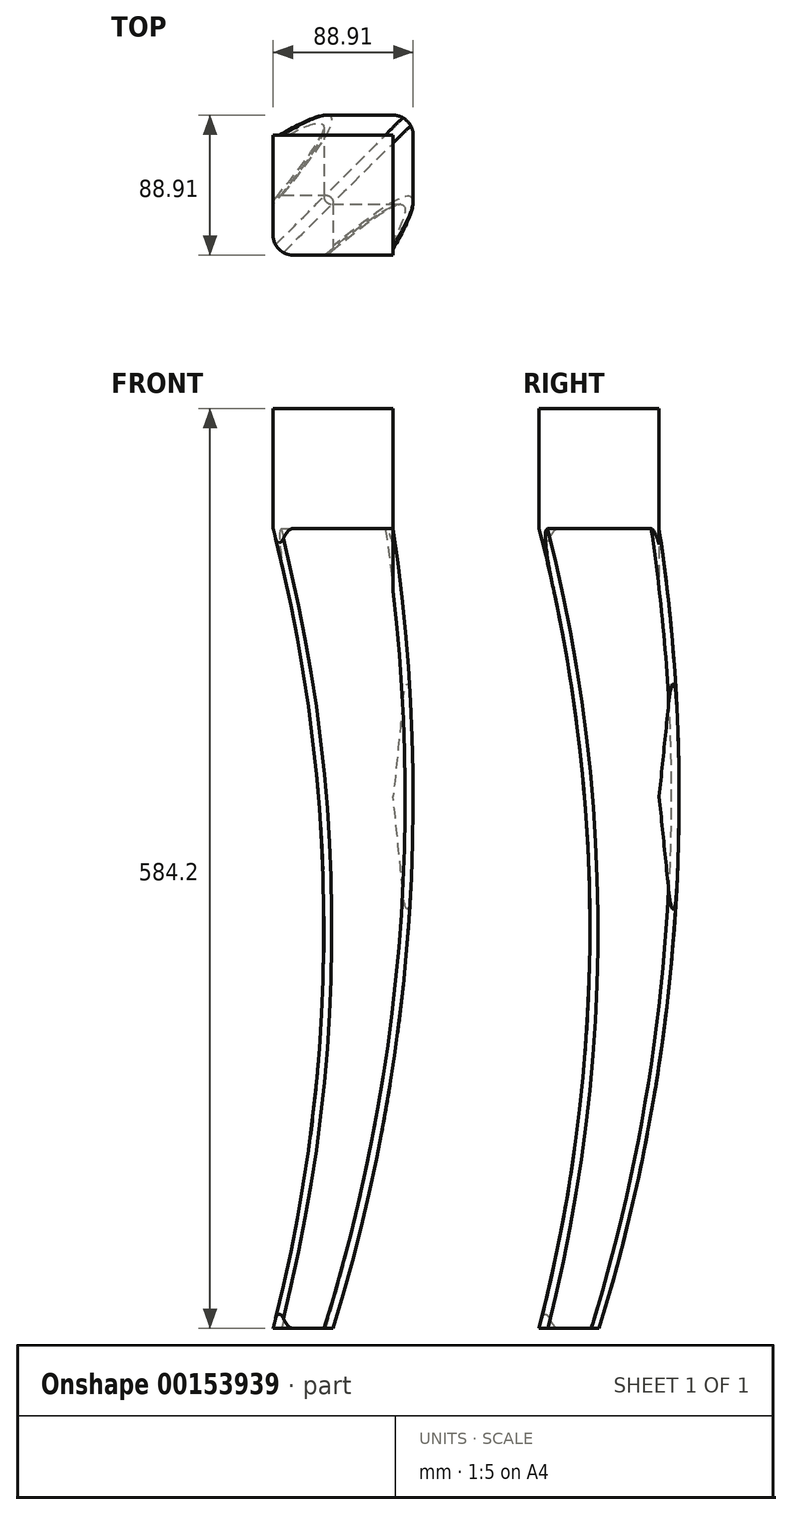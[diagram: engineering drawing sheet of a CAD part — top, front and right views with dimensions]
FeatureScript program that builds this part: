
annotation { "Feature Type Name" : "Feature", "Feature Type Description" : "" }
export const myFeature = defineFeature(function(context is Context, id is Id, definition is map)
    precondition{}
    {
        {
            var Q0;
            Q0=qCreatedBy(makeId("Top.planeOp"),FACE);
            var sketch = newSketch(context, id + "F0", { "sketchPlane" : qUnion([Q0])});
            skLineSegment(sketch, "E0.bottom", {"start": v(31.75, -44.45) * mm, "end": v(-31.75, -44.45) * mm});
            skLineSegment(sketch, "E0.top", {"start": v(31.75, 44.45) * mm, "end": v(-31.75, 44.45) * mm});
            skLineSegment(sketch, "E0.left", {"start": v(44.45, -31.75) * mm, "end": v(44.45, 31.75) * mm});
            skLineSegment(sketch, "E0.right", {"start": v(-44.45, -31.75) * mm, "end": v(-44.45, 31.75) * mm});
            skPoint(sketch, "E0.middle", {"position": v(0, 0) * mm});
            skPoint(sketch, "E1.visualSharp", {"position": v(44.45, -44.45) * mm});
            skArc(sketch, "E1.filletArc", {"start": v(31.75, -44.45) * mm, "mid": v(40.73, -40.73) * mm, "end": v(44.45, -31.75) * mm});
            skPoint(sketch, "E2.visualSharp", {"position": v(44.45, 44.45) * mm});
            skArc(sketch, "E2.filletArc", {"start": v(44.45, 31.75) * mm, "mid": v(40.73, 40.73) * mm, "end": v(31.75, 44.45) * mm});
            skPoint(sketch, "E3.visualSharp", {"position": v(-44.45, 44.45) * mm});
            skArc(sketch, "E3.filletArc", {"start": v(-31.75, 44.45) * mm, "mid": v(-40.73, 40.73) * mm, "end": v(-44.45, 31.75) * mm});
            skPoint(sketch, "E4.visualSharp", {"position": v(-44.45, -44.45) * mm});
            skArc(sketch, "E4.filletArc", {"start": v(-44.45, -31.75) * mm, "mid": v(-40.73, -40.73) * mm, "end": v(-31.75, -44.45) * mm});
            skSolve(sketch);
        }
        {
            var Q0;
            Q0 = qSketchRegion(id + "F0", true);
            extrude(context, id + "F1", {"entities" : qUnion([Q0]), "depth" : 584.2 * mm});
        }
        {
            var Q0;
            Q0=makeQuery(id+"F1.opExtrude","SWEPT_FACE",FACE,{"disambiguationData":[OSD([sQuery(id+"F0.wireOp",EDGE,"E0.left")])]});
            var sketch = newSketch(context, id + "F2", { "sketchPlane" : qUnion([Q0])});
            skArc(sketch, "E5", {"start": v(-44.45, 0) * mm, "mid": v(-12.19, 254) * mm, "end": v(-44.45, 508) * mm});
            skArc(sketch, "E6", {"start": v(-6.35, 0) * mm, "mid": v(41.23, 251.86) * mm, "end": v(31.75, 508) * mm});
            skLineSegment(sketch, "E7", {"start": v(-44.45, 0) * mm, "end": v(-6.35, 0) * mm, "construction": true});
            skLineSegment(sketch, "E8", {"start": v(-44.45, 508) * mm, "end": v(-44.45, 584.2) * mm});
            skLineSegment(sketch, "E9", {"start": v(-44.45, 584.2) * mm, "end": v(31.75, 584.2) * mm, "construction": true});
            skLineSegment(sketch, "E10", {"start": v(31.75, 508) * mm, "end": v(31.75, 584.2) * mm});
            skLineSegment(sketch, "E11", {"start": v(-44.45, 508) * mm, "end": v(31.75, 508) * mm, "construction": true});
            skLineSegment(sketch, "E12", {"start": v(31.75, 584.2) * mm, "end": v(100.82, 584.2) * mm});
            skLineSegment(sketch, "E13", {"start": v(100.82, 584.2) * mm, "end": v(100.82, 0) * mm});
            skLineSegment(sketch, "E14", {"start": v(100.82, 0) * mm, "end": v(-6.35, 0) * mm});
            skLineSegment(sketch, "E15", {"start": v(-44.45, 0) * mm, "end": v(-95.04, 0) * mm});
            skLineSegment(sketch, "E16", {"start": v(-95.04, 0) * mm, "end": v(-95.04, 584.2) * mm});
            skLineSegment(sketch, "E17", {"start": v(-95.04, 584.2) * mm, "end": v(-31.75, 584.2) * mm});
            skSolve(sketch);
        }
        {
            var Q0;
            Q0 = qSketchRegion(id + "F2", true);
            extrude(context, id + "F3", {"entities" : qUnion([Q0]), "operationType" : NewBodyOperationType.REMOVE, "oppositeDirection" : true, "depth" : 101.6 * mm});
        }
        {
            var Q0;
            Q0=makeQuery(id+"F1.opExtrude","SWEPT_FACE",FACE,{"disambiguationData":[OSD([sQuery(id+"F0.wireOp",EDGE,"E0.bottom")])]});
            var sketch = newSketch(context, id + "F4", { "sketchPlane" : qUnion([Q0])});
            skArc(sketch, "E18", {"start": v(-44.45, 0) * mm, "mid": v(-12.19, 254) * mm, "end": v(-44.45, 508) * mm});
            skArc(sketch, "E19", {"start": v(-6.35, 0) * mm, "mid": v(41.23, 251.86) * mm, "end": v(31.75, 508) * mm});
            skLineSegment(sketch, "E20", {"start": v(-44.45, 0) * mm, "end": v(-6.35, 0) * mm, "construction": true});
            skLineSegment(sketch, "E21", {"start": v(-44.45, 508) * mm, "end": v(-44.45, 584.2) * mm});
            skLineSegment(sketch, "E22", {"start": v(-44.45, 584.2) * mm, "end": v(31.75, 584.2) * mm, "construction": true});
            skLineSegment(sketch, "E23", {"start": v(31.75, 508) * mm, "end": v(31.75, 584.2) * mm});
            skLineSegment(sketch, "E24", {"start": v(-44.45, 508) * mm, "end": v(31.75, 508) * mm, "construction": true});
            skLineSegment(sketch, "E25", {"start": v(31.75, 584.2) * mm, "end": v(100.82, 584.2) * mm});
            skLineSegment(sketch, "E26", {"start": v(100.82, 584.2) * mm, "end": v(100.82, 0) * mm});
            skLineSegment(sketch, "E27", {"start": v(100.82, 0) * mm, "end": v(-6.35, 0) * mm});
            skLineSegment(sketch, "E28", {"start": v(-44.45, 0) * mm, "end": v(-207.88, 0) * mm});
            skLineSegment(sketch, "E29", {"start": v(-207.88, 0) * mm, "end": v(-207.88, 584.2) * mm});
            skLineSegment(sketch, "E30", {"start": v(-207.88, 584.2) * mm, "end": v(-44.45, 584.2) * mm});
            skSolve(sketch);
        }
        {
            var Q0;
            Q0 = qSketchRegion(id + "F4", true);
            extrude(context, id + "F5", {"entities" : qUnion([Q0]), "operationType" : NewBodyOperationType.REMOVE, "endBound" : BoundingType.THROUGH_ALL, "oppositeDirection" : true, "depth" : 25.4 * mm});
        }
        {
            var Q0;
            Q0=makeQuery(id+"F5.boolean.opBoolean","INTERSECT",EDGE,{"disambiguationData":[OD(0.0)],"derivedFrom":[makeQuery(id+"F3.boolean.opBoolean","COPY",FACE,{"derivedFrom":makeQuery(id+"F3.opExtrude","SWEPT_FACE",FACE,{"disambiguationData":[OSD([sQuery(id+"F2.wireOp",EDGE,"E6")])]})}),makeQuery(id+"F5.opExtrude","SWEPT_FACE",FACE,{"disambiguationData":[OSD([sQuery(id+"F4.wireOp",EDGE,"E19")])]})]});
            var Q1;
            Q1=makeQuery(id+"F5.boolean.opBoolean","INTERSECT",EDGE,{"disambiguationData":[OD(1.0)],"derivedFrom":[makeQuery(id+"F3.boolean.opBoolean","COPY",FACE,{"derivedFrom":makeQuery(id+"F3.opExtrude","SWEPT_FACE",FACE,{"disambiguationData":[OSD([sQuery(id+"F2.wireOp",EDGE,"E6")])]})}),makeQuery(id+"F5.opExtrude","SWEPT_FACE",FACE,{"disambiguationData":[OSD([sQuery(id+"F4.wireOp",EDGE,"E19")])]})]});
            var Q2;
            Q2=makeQuery(id+"F5.boolean.opBoolean","INTERSECT",EDGE,{"derivedFrom":[makeQuery(id+"F3.boolean.opBoolean","COPY",FACE,{"derivedFrom":makeQuery(id+"F3.opExtrude","SWEPT_FACE",FACE,{"disambiguationData":[OSD([sQuery(id+"F2.wireOp",EDGE,"E6")])]})}),makeQuery(id+"F5.opExtrude","SWEPT_FACE",FACE,{"disambiguationData":[OSD([sQuery(id+"F4.wireOp",EDGE,"E18")])]})]});
            var Q3;
            Q3=makeQuery(id+"F5.boolean.opBoolean","INTERSECT",EDGE,{"derivedFrom":[makeQuery(id+"F3.boolean.opBoolean","COPY",FACE,{"derivedFrom":makeQuery(id+"F3.opExtrude","SWEPT_FACE",FACE,{"disambiguationData":[OSD([sQuery(id+"F2.wireOp",EDGE,"E5")])]})}),makeQuery(id+"F5.opExtrude","SWEPT_FACE",FACE,{"disambiguationData":[OSD([sQuery(id+"F4.wireOp",EDGE,"E18")])]})]});
            var Q4;
            Q4=makeQuery(id+"F5.boolean.opBoolean","INTERSECT",EDGE,{"derivedFrom":[makeQuery(id+"F3.boolean.opBoolean","COPY",FACE,{"derivedFrom":makeQuery(id+"F3.opExtrude","SWEPT_FACE",FACE,{"disambiguationData":[OSD([sQuery(id+"F2.wireOp",EDGE,"E5")])]})}),makeQuery(id+"F5.opExtrude","SWEPT_FACE",FACE,{"disambiguationData":[OSD([sQuery(id+"F4.wireOp",EDGE,"E19")])]})]});
            fillet(context, id + "F6", {"entities" : qUnion([Q0, Q1, Q2, Q3, Q4]), "radius" : 5.08 * mm, "tangentPropagation" : true, "allowEdgeOverflow" : false});
        }
    });
